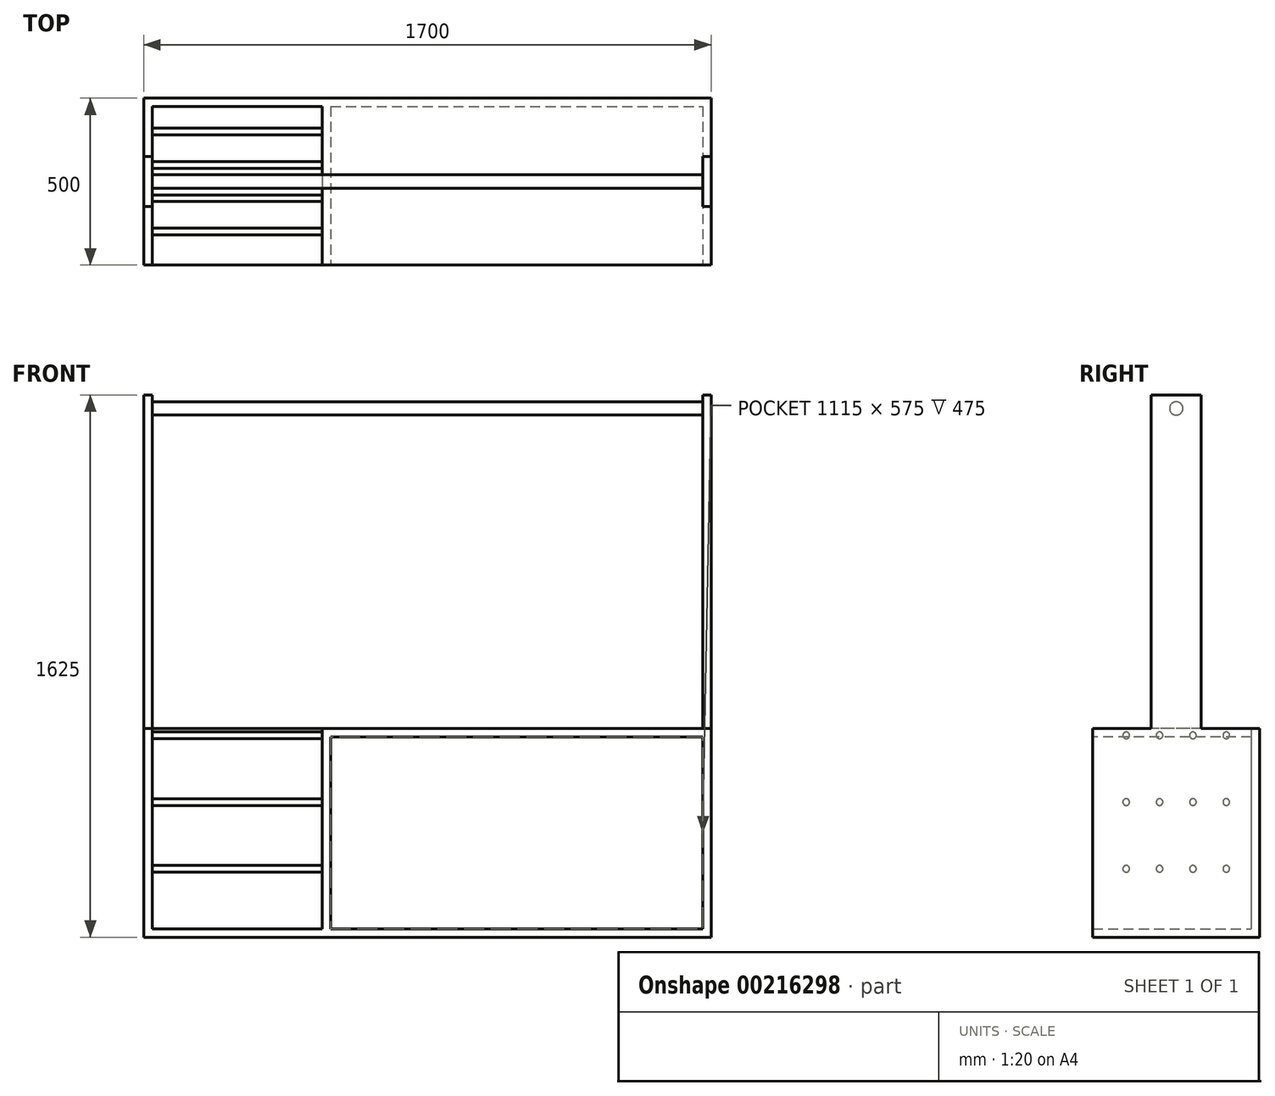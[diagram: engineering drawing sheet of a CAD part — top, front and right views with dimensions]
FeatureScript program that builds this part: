
annotation { "Feature Type Name" : "Feature", "Feature Type Description" : "" }
export const myFeature = defineFeature(function(context is Context, id is Id, definition is map)
    precondition{}
    {
        {
            var Q0;
            Q0=qCreatedBy(makeId("Top.planeOp"),FACE);
            var sketch = newSketch(context, id + "F0", { "sketchPlane" : qUnion([Q0])});
            skLineSegment(sketch, "E0.bottom", {"start": v(0, 0) * mm, "end": v(1700, 0) * mm});
            skLineSegment(sketch, "E0.top", {"start": v(0, 500) * mm, "end": v(1700, 500) * mm});
            skLineSegment(sketch, "E0.left", {"start": v(0, 0) * mm, "end": v(0, 500) * mm});
            skLineSegment(sketch, "E0.right", {"start": v(1700, 0) * mm, "end": v(1700, 500) * mm});
            skSolve(sketch);
        }
        {
            var Q0;
            Q0 = qSketchRegion(id + "F0", true);
            extrude(context, id + "F1", {"entities" : qUnion([Q0]), "depth" : 25 * mm});
        }
        {
            var Q0;
            Q0=makeQuery(id+"F1.opExtrude","CAP_FACE",FACE,{"disambiguationData":[OSD([sQuery(id+"F0.wireOp",EDGE,"E0.bottom"),sQuery(id+"F0.wireOp",EDGE,"E0.top"),sQuery(id+"F0.wireOp",EDGE,"E0.left"),sQuery(id+"F0.wireOp",EDGE,"E0.right")])],"isStart":false});
            var sketch = newSketch(context, id + "F2", { "sketchPlane" : qUnion([Q0])});
            skLineSegment(sketch, "E1.bottom", {"start": v(0, 0) * mm, "end": v(25, 0) * mm});
            skLineSegment(sketch, "E1.top", {"start": v(0, 500) * mm, "end": v(25, 500) * mm});
            skLineSegment(sketch, "E1.left", {"start": v(0, 0) * mm, "end": v(0, 500) * mm});
            skLineSegment(sketch, "E1.right", {"start": v(25, 0) * mm, "end": v(25, 500) * mm});
            skSolve(sketch);
        }
        {
            var Q0;
            Q0 = qSketchRegion(id + "F2", true);
            extrude(context, id + "F3", {"entities" : qUnion([Q0]), "operationType" : NewBodyOperationType.ADD, "depth" : 600 * mm});
        }
        {
            var Q0;
            Q0=qCreatedBy(makeId("Right.planeOp"),FACE);
            cPlane(context, id + "F4", {"entities" : qUnion([Q0]), "cplaneType" : CPlaneType.OFFSET, "offset" : (1700 / 2) * mm, "width" : 150 * mm, "height" : 150 * mm});
        }
        {
            var Q0;
            Q0=makeQuery(id+"F1.opExtrude","SWEPT_BODY",BODY,{"disambiguationData":[OSD([sQuery(id+"F0.wireOp",EDGE,"E0.bottom"),sQuery(id+"F0.wireOp",EDGE,"E0.top"),sQuery(id+"F0.wireOp",EDGE,"E0.left"),sQuery(id+"F0.wireOp",EDGE,"E0.right")])]});
            var Q1;
            Q1=qCreatedBy(id+"F4.planeOp",FACE);
            mirror(context, id + "F5", {"operationType" : NewBodyOperationType.ADD, "entities" : qUnion([Q0]), "mirrorPlane" : qUnion([Q1])});
        }
        {
            var Q0;
            Q0=makeQuery(id+"F1.opExtrude","CAP_FACE",FACE,{"disambiguationData":[OSD([sQuery(id+"F0.wireOp",EDGE,"E0.bottom"),sQuery(id+"F0.wireOp",EDGE,"E0.top"),sQuery(id+"F0.wireOp",EDGE,"E0.left"),sQuery(id+"F0.wireOp",EDGE,"E0.right")])],"isStart":false});
            var sketch = newSketch(context, id + "F6", { "sketchPlane" : qUnion([Q0])});
            skLineSegment(sketch, "E2.bottom", {"start": v(25, 500) * mm, "end": v(1675, 500) * mm});
            skLineSegment(sketch, "E2.top", {"start": v(25, 475) * mm, "end": v(1675, 475) * mm});
            skLineSegment(sketch, "E2.left", {"start": v(25, 500) * mm, "end": v(25, 475) * mm});
            skLineSegment(sketch, "E2.right", {"start": v(1675, 500) * mm, "end": v(1675, 475) * mm});
            skSolve(sketch);
        }
        {
            var Q0;
            Q0 = qSketchRegion(id + "F6", true);
            var Q1;
            Q1=makeQuery(id+"F3.opExtrude","CAP_FACE",FACE,{"disambiguationData":[OSD([sQuery(id+"F2.wireOp",EDGE,"E1.bottom"),sQuery(id+"F2.wireOp",EDGE,"E1.top"),sQuery(id+"F2.wireOp",EDGE,"E1.left"),sQuery(id+"F2.wireOp",EDGE,"E1.right")])],"isStart":false});
            extrude(context, id + "F7", {"entities" : qUnion([Q0]), "operationType" : NewBodyOperationType.ADD, "endBound" : BoundingType.UP_TO_SURFACE, "endBoundEntityFace" : qUnion([Q1]), "depth" : 25 * mm});
        }
        {
            var Q0;
            Q0=makeQuery(id+"F1.opExtrude","CAP_FACE",FACE,{"disambiguationData":[OSD([sQuery(id+"F0.wireOp",EDGE,"E0.bottom"),sQuery(id+"F0.wireOp",EDGE,"E0.top"),sQuery(id+"F0.wireOp",EDGE,"E0.left"),sQuery(id+"F0.wireOp",EDGE,"E0.right")])],"isStart":false});
            var sketch = newSketch(context, id + "F8", { "sketchPlane" : qUnion([Q0])});
            skLineSegment(sketch, "E3.bottom", {"start": v(535, 475) * mm, "end": v(560, 475) * mm});
            skLineSegment(sketch, "E3.top", {"start": v(535, 0) * mm, "end": v(560, 0) * mm});
            skLineSegment(sketch, "E3.left", {"start": v(535, 475) * mm, "end": v(535, 0) * mm});
            skLineSegment(sketch, "E3.right", {"start": v(560, 475) * mm, "end": v(560, 0) * mm});
            skSolve(sketch);
        }
        {
            var Q0;
            Q0 = qSketchRegion(id + "F8", true);
            var Q1;
            {var subQ0=sQuery(id+"F2.wireOp",EDGE,"E1.right");var subQ1=sQuery(id+"F2.wireOp",EDGE,"E1.left");var subQ2=sQuery(id+"F2.wireOp",EDGE,"E1.top");var subQ3=sQuery(id+"F2.wireOp",EDGE,"E1.bottom");var subQ4=makeQuery(id+"F3.opExtrude","CAP_FACE",FACE,{"disambiguationData":[OSD([subQ3,subQ2,subQ1,subQ0])],"isStart":false});Q1=makeQuery(id+"F7.boolean.opBoolean","MERGE",FACE,{"derivedFrom":[subQ4,makeQuery(id+"F5.opPattern","COPY",FACE,{"derivedFrom":subQ4,"instanceName":"1"}),makeQuery(id+"F7.opExtrude","CAP_FACE",FACE,{"disambiguationData":[OSD([subQ3,subQ2,subQ1,subQ0])],"isStart":false})]});}
            extrude(context, id + "F9", {"entities" : qUnion([Q0]), "operationType" : NewBodyOperationType.ADD, "endBound" : BoundingType.UP_TO_SURFACE, "endBoundEntityFace" : qUnion([Q1]), "depth" : 25 * mm});
        }
        {
            var Q0;
            {var subQ0=sQuery(id+"F2.wireOp",EDGE,"E1.right");var subQ1=sQuery(id+"F2.wireOp",EDGE,"E1.left");var subQ2=sQuery(id+"F2.wireOp",EDGE,"E1.top");var subQ3=sQuery(id+"F2.wireOp",EDGE,"E1.bottom");var subQ4=makeQuery(id+"F3.opExtrude","CAP_FACE",FACE,{"disambiguationData":[OSD([subQ3,subQ2,subQ1,subQ0])],"isStart":false});Q0=makeQuery(id+"F9.boolean.opBoolean","MERGE",FACE,{"derivedFrom":[makeQuery(id+"F7.boolean.opBoolean","MERGE",FACE,{"derivedFrom":[subQ4,makeQuery(id+"F5.opPattern","COPY",FACE,{"derivedFrom":subQ4,"instanceName":"1"}),makeQuery(id+"F7.opExtrude","CAP_FACE",FACE,{"disambiguationData":[OSD([subQ3,subQ2,subQ1,subQ0])],"isStart":false})]}),makeQuery(id+"F9.opExtrude","CAP_FACE",FACE,{"disambiguationData":[OSD([subQ3,subQ2,subQ1,subQ0])],"isStart":false})]});}
            var sketch = newSketch(context, id + "F10", { "sketchPlane" : qUnion([Q0])});
            skLineSegment(sketch, "E4.bottom", {"start": v(535, 0) * mm, "end": v(1700, 0) * mm});
            skLineSegment(sketch, "E4.top", {"start": v(535, 500) * mm, "end": v(1700, 500) * mm});
            skLineSegment(sketch, "E4.left", {"start": v(535, 0) * mm, "end": v(535, 500) * mm});
            skLineSegment(sketch, "E4.right", {"start": v(1700, 0) * mm, "end": v(1700, 500) * mm});
            skSolve(sketch);
        }
        {
            var Q0;
            Q0 = qSketchRegion(id + "F10", true);
            extrude(context, id + "F11", {"entities" : qUnion([Q0]), "operationType" : NewBodyOperationType.ADD, "oppositeDirection" : true, "depth" : 25 * mm});
        }
        {
            var Q0;
            Q0=makeQuery(id+"F3.opExtrude","SWEPT_FACE",FACE,{"disambiguationData":[OSD([sQuery(id+"F2.wireOp",EDGE,"E1.right")])]});
            var sketch = newSketch(context, id + "F12", { "sketchPlane" : qUnion([Q0])});
            skCircle(sketch, "E5", {"center": v(100, 605) * mm, "radius": 10 * mm});
            skCircle(sketch, "E6.0.2.0", {"center": v(100, 205) * mm, "radius": 10 * mm});
            skCircle(sketch, "E7.0.1.0", {"center": v(100, 405) * mm, "radius": 10 * mm});
            skCircle(sketch, "E7.1.0.0", {"center": v(200, 605) * mm, "radius": 10 * mm});
            skCircle(sketch, "E7.1.1.0", {"center": v(200, 405) * mm, "radius": 10 * mm});
            skCircle(sketch, "E7.1.2.0", {"center": v(200, 205) * mm, "radius": 10 * mm});
            skCircle(sketch, "E7.2.0.0", {"center": v(300, 605) * mm, "radius": 10 * mm});
            skCircle(sketch, "E7.2.1.0", {"center": v(300, 405) * mm, "radius": 10 * mm});
            skCircle(sketch, "E7.2.2.0", {"center": v(300, 205) * mm, "radius": 10 * mm});
            skCircle(sketch, "E7.3.0.0", {"center": v(400, 605) * mm, "radius": 10 * mm});
            skCircle(sketch, "E7.3.1.0", {"center": v(400, 405) * mm, "radius": 10 * mm});
            skCircle(sketch, "E7.3.2.0", {"center": v(400, 205) * mm, "radius": 10 * mm});
            skLineSegment(sketch, "E7.direction1", {"start": v(100, 605) * mm, "end": v(200, 605) * mm, "construction": true});
            skLineSegment(sketch, "E7.direction2", {"start": v(100, 605) * mm, "end": v(100, 405) * mm, "construction": true});
            skSolve(sketch);
        }
        {
            var Q0;
            Q0 = qSketchRegion(id + "F12", true);
            extrude(context, id + "F13", {"entities" : qUnion([Q0]), "operationType" : NewBodyOperationType.ADD, "endBound" : BoundingType.UP_TO_NEXT, "depth" : 25 * mm});
        }
        {
            var Q0;
            {var subQ0=sQuery(id+"F2.wireOp",EDGE,"E1.right");var subQ1=sQuery(id+"F2.wireOp",EDGE,"E1.left");var subQ2=sQuery(id+"F2.wireOp",EDGE,"E1.top");var subQ3=sQuery(id+"F2.wireOp",EDGE,"E1.bottom");var subQ4=makeQuery(id+"F3.opExtrude","CAP_FACE",FACE,{"disambiguationData":[OSD([subQ3,subQ2,subQ1,subQ0])],"isStart":false});Q0=makeQuery(id+"F11.boolean.opBoolean","MERGE",FACE,{"derivedFrom":[makeQuery(id+"F9.boolean.opBoolean","MERGE",FACE,{"derivedFrom":[makeQuery(id+"F7.boolean.opBoolean","MERGE",FACE,{"derivedFrom":[subQ4,makeQuery(id+"F5.opPattern","COPY",FACE,{"derivedFrom":subQ4,"instanceName":"1"}),makeQuery(id+"F7.opExtrude","CAP_FACE",FACE,{"disambiguationData":[OSD([subQ3,subQ2,subQ1,subQ0])],"isStart":false})]}),makeQuery(id+"F9.opExtrude","CAP_FACE",FACE,{"disambiguationData":[OSD([subQ3,subQ2,subQ1,subQ0])],"isStart":false})]}),makeQuery(id+"F11.opExtrude","CAP_FACE",FACE,{"disambiguationData":[OSD([sQuery(id+"F10.wireOp",EDGE,"E4.bottom"),sQuery(id+"F10.wireOp",EDGE,"E4.top"),sQuery(id+"F10.wireOp",EDGE,"E4.left"),sQuery(id+"F10.wireOp",EDGE,"E4.right")])],"isStart":true})]});}
            var sketch = newSketch(context, id + "F14", { "sketchPlane" : qUnion([Q0])});
            skLineSegment(sketch, "E8.bottom", {"start": v(0, 175) * mm, "end": v(25, 175) * mm});
            skLineSegment(sketch, "E8.top", {"start": v(0, 325) * mm, "end": v(25, 325) * mm});
            skLineSegment(sketch, "E8.left", {"start": v(0, 175) * mm, "end": v(0, 325) * mm});
            skLineSegment(sketch, "E8.right", {"start": v(25, 175) * mm, "end": v(25, 325) * mm});
            skSolve(sketch);
        }
        {
            var Q0;
            Q0 = qSketchRegion(id + "F14", true);
            extrude(context, id + "F15", {"entities" : qUnion([Q0]), "operationType" : NewBodyOperationType.ADD, "depth" : 1000 * mm});
        }
        {
            var Q0;
            {var subQ0=sQuery(id+"F2.wireOp",EDGE,"E1.top");var subQ2=makeQuery(id+"F1.opExtrude","SWEPT_FACE",FACE,{"disambiguationData":[OSD([sQuery(id+"F0.wireOp",EDGE,"E0.top")])]});var subQ3=sQuery(id+"F2.wireOp",EDGE,"E1.right");var subQ4=sQuery(id+"F2.wireOp",EDGE,"E1.left");var subQ7=sQuery(id+"F2.wireOp",EDGE,"E1.bottom");var subQ10=sQuery(id+"F10.wireOp",EDGE,"E4.bottom");var subQ11=makeQuery(id+"F3.opExtrude","CAP_FACE",FACE,{"disambiguationData":[OSD([subQ7,subQ0,subQ4,subQ3])],"isStart":false});Q0=makeQuery(id+"F15.boolean.opBoolean","SPLIT",FACE,{"disambiguationData":[TD([subQ2])],"derivedFrom":makeQuery(id+"F11.boolean.opBoolean","MERGE",FACE,{"derivedFrom":[makeQuery(id+"F9.boolean.opBoolean","MERGE",FACE,{"derivedFrom":[makeQuery(id+"F7.boolean.opBoolean","MERGE",FACE,{"derivedFrom":[subQ11,makeQuery(id+"F5.opPattern","COPY",FACE,{"derivedFrom":subQ11,"instanceName":"1"}),makeQuery(id+"F7.opExtrude","CAP_FACE",FACE,{"disambiguationData":[OSD([subQ7,subQ0,subQ4,subQ3])],"isStart":false})]}),makeQuery(id+"F9.opExtrude","CAP_FACE",FACE,{"disambiguationData":[OSD([subQ7,subQ0,subQ4,subQ3])],"isStart":false})]}),makeQuery(id+"F11.opExtrude","CAP_FACE",FACE,{"disambiguationData":[OSD([subQ10,sQuery(id+"F10.wireOp",EDGE,"E4.top"),sQuery(id+"F10.wireOp",EDGE,"E4.left"),sQuery(id+"F10.wireOp",EDGE,"E4.right")])],"isStart":true})]})});}
            var sketch = newSketch(context, id + "F16", { "sketchPlane" : qUnion([Q0])});
            skLineSegment(sketch, "E9.bottom", {"start": v(1700, 325) * mm, "end": v(1675, 325) * mm});
            skLineSegment(sketch, "E9.top", {"start": v(1700, 175) * mm, "end": v(1675, 175) * mm});
            skLineSegment(sketch, "E9.left", {"start": v(1700, 325) * mm, "end": v(1700, 175) * mm});
            skLineSegment(sketch, "E9.right", {"start": v(1675, 325) * mm, "end": v(1675, 175) * mm});
            skSolve(sketch);
        }
        {
            var Q0;
            Q0 = qSketchRegion(id + "F16", true);
            extrude(context, id + "F17", {"entities" : qUnion([Q0]), "operationType" : NewBodyOperationType.ADD, "depth" : 1000 * mm});
        }
        {
            var Q0;
            Q0=makeQuery(id+"F15.boolean.opBoolean","MERGE",FACE,{"derivedFrom":[makeQuery(id+"F3.opExtrude","SWEPT_FACE",FACE,{"disambiguationData":[OSD([sQuery(id+"F2.wireOp",EDGE,"E1.right")])]}),makeQuery(id+"F15.opExtrude","SWEPT_FACE",FACE,{"disambiguationData":[OSD([sQuery(id+"F14.wireOp",EDGE,"E8.right")])]})]});
            var sketch = newSketch(context, id + "F18", { "sketchPlane" : qUnion([Q0])});
            skCircle(sketch, "E10", {"center": v(250, 1585) * mm, "radius": 20 * mm});
            skSolve(sketch);
        }
        {
            var Q0;
            Q0 = qSketchRegion(id + "F18", true);
            extrude(context, id + "F19", {"entities" : qUnion([Q0]), "operationType" : NewBodyOperationType.ADD, "endBound" : BoundingType.UP_TO_NEXT, "depth" : 25 * mm});
        }
    });
